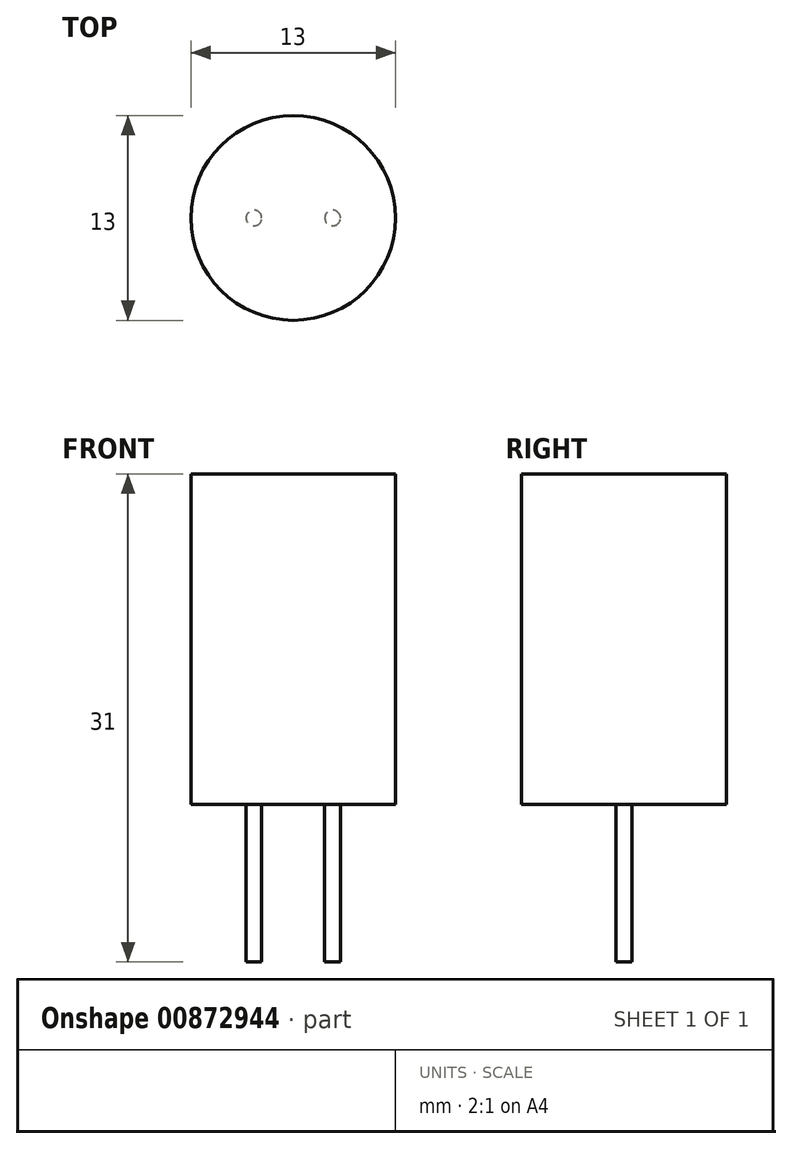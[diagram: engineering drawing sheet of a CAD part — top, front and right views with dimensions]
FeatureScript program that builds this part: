
annotation { "Feature Type Name" : "Feature", "Feature Type Description" : "" }
export const myFeature = defineFeature(function(context is Context, id is Id, definition is map)
    precondition{}
    {
        {
            var Q0;
            Q0=qCreatedBy(makeId("Top.planeOp"),FACE);
            var sketch = newSketch(context, id + "F0", { "sketchPlane" : qUnion([Q0])});
            skCircle(sketch, "E0", {"center": v(0, 0) * mm, "radius": 6.5 * mm});
            skSolve(sketch);
        }
        {
            var Q0;
            Q0 = qSketchRegion(id + "F0", true);
            extrude(context, id + "F1", {"entities" : qUnion([Q0]), "depth" : 21 * mm, "offsetDistance" : 25 * mm});
        }
        {
            var Q0;
            Q0=qCreatedBy(makeId("Top.planeOp"),FACE);
            var sketch = newSketch(context, id + "F2", { "sketchPlane" : qUnion([Q0])});
            skCircle(sketch, "E1", {"center": v(-2.5, 0) * mm, "radius": 0.5 * mm});
            skCircle(sketch, "E2.MirrorC", {"center": v(2.5, 0) * mm, "radius": 0.5 * mm});
            skSolve(sketch);
        }
        {
            var Q0;
            Q0 = qSketchRegion(id + "F2", true);
            extrude(context, id + "F3", {"entities" : qUnion([Q0]), "operationType" : NewBodyOperationType.ADD, "oppositeDirection" : true, "depth" : 10 * mm, "offsetDistance" : 25 * mm});
        }
    });
